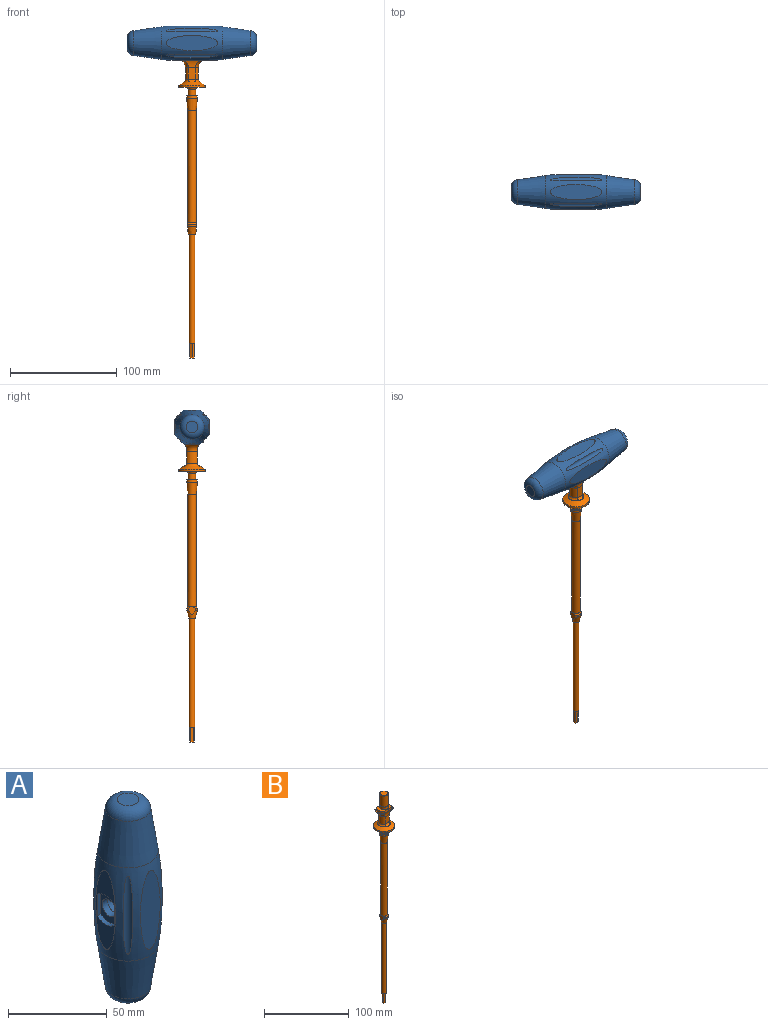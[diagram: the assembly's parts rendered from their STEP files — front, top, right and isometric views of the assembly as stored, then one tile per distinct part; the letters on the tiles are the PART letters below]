
ASSEMBLY  parts=2 mates=1
PART A: 25 faces, bbox 35x35x121 mm
  f0: plane 48.53x14.18mm, normal (-1,0,0), area 338.1mm2, adj f1,f15,f16,f17,f18
  f1: revolved ~57.74x35mm, area 3072.3mm2, adj f0,f2,f3,f8,f9,f10,f11,f12
  f2: cone r=15.37mm half-angle=8.4deg, axis (0,0,1), area 2230mm2, adj f1,f7
  f3: cone r=15.37mm half-angle=8.4deg, axis (0,0,-1), area 2230mm2, adj f1,f4
  f4: torus R=5.5mm, axis (0,0,-1), area 517mm2, adj f3,f5
  f5: plane 11x11mm, normal (0,0,1), area 95mm2, adj f4
  f6: plane 11x11mm, normal (0,0,-1), area 95mm2, adj f7
  f7: torus R=5.5mm, axis (0,0,-1), area 517mm2, adj f2,f6
  f8: plane 48.53x14.18mm, normal (1,0,0), area 537.4mm2, adj f1
  f9: plane 48.53x14.18mm, normal (0,-1,0), area 539.1mm2, adj f1
  f10: plane 48.53x14.18mm, normal (0,1,0), area 539.1mm2, adj f1
  f11: cylinder r=3mm len=48.57mm, axis (0,0,-1), area 218.5mm2, adj f1
  f12: cylinder r=3mm len=48.54mm, axis (0,0,-1), area 216.3mm2, adj f1
  f13: cylinder r=3mm len=48.56mm, axis (0,0,-1), area 221.5mm2, adj f1
  f14: cylinder r=3mm len=48.59mm, axis (0,0,-1), area 220.2mm2, adj f1
  f15: plane 13.18x2.5mm, normal (0,1,0), area 33mm2, adj f0,f16,f18,f19
  f16: cylinder r=8.98mm len=12.1mm, axis (-1,0,0), area 33.2mm2, adj f0,f15,f17,f19
  f17: plane 13.36x2.5mm, normal (0,-1,0), area 33.4mm2, adj f0,f16,f18,f19
  f18: cylinder r=8.98mm len=12.1mm, axis (-1,0,0), area 33.2mm2, adj f0,f15,f17,f19
  f19: plane 17.96x12.1mm, normal (-1,0,0), area 121mm2, adj f15,f16,f17,f18,f20
  f20: cylinder r=5mm len=10mm, axis (-1,0,0), area 125.7mm2, adj f19,f21
  f21: plane 10.25x10.25mm, normal (1,0,0), area 4mm2, adj f20,f22
  f22: cylinder r=5.12mm len=16mm, axis (-1,0,0), area 515.2mm2, adj f21,f23
  f23: cone r=4.5mm half-angle=51.3deg, axis (-1,0,0), area 24.2mm2, adj f22,f24
  f24: plane 9x9mm, normal (-1,0,0), area 63.6mm2, adj f23
PART B: 52 faces, bbox 30.3x26.3x303.4 mm
  f0: torus R=9mm, axis (0,0,1), area 52mm2, adj f8,f26,f39,f42
  f1: cylinder r=6mm len=11mm, axis (0,0,1), area 130mm2, adj f7,f9,f35,f40
  f2: torus R=13.4mm, axis (0,0,1), area 112.5mm2, adj f8,f10,f38,f43
  f3: plane 13.19x4.83mm, normal (0,0,1), area 28.7mm2, adj f4,f9,f36,f38,f43,f44
  f4: cylinder r=8.98mm len=12.02mm, axis (0,0,1), area 32.9mm2, adj f3,f6,f37,f41
  f5: cylinder r=8.98mm len=12.02mm, axis (0,0,1), area 32.9mm2, adj f6,f10,f37,f41
  f6: plane 17.96x12.02mm, normal (0,0,1), area 119.9mm2, adj f4,f5,f27,f37,f41
  f7: torus R=9mm, axis (0,0,1), area 52mm2, adj f1,f26,f39,f42
  f8: cylinder r=6mm len=11mm, axis (0,0,1), area 130mm2, adj f0,f2,f35,f40
  f9: torus R=13.4mm, axis (0,0,1), area 112.5mm2, adj f1,f3,f38,f43
  f10: plane 13.19x4.83mm, normal (0,0,1), area 28.7mm2, adj f2,f5,f36,f38,f43,f44
  f11: cone r=5mm half-angle=14deg, axis (0,0,1), area 178mm2, adj f12,f13,f17,f33,f34
  f12: cylinder r=5mm len=8mm, axis (0,0,1), area 18.5mm2, adj f11,f15,f33,f34
  f13: cylinder r=5mm len=8mm, axis (0,0,1), area 18.5mm2, adj f11,f14,f33,f34
  f14: cone r=4mm half-angle=33.7deg, axis (0,0,-1), area 20.1mm2, adj f13,f18,f33,f34
  f15: cone r=4mm half-angle=33.7deg, axis (0,0,-1), area 20.1mm2, adj f12,f18,f33,f34
  f16: cylinder r=2.7mm len=102mm, axis (0,0,1), area 1730.4mm2, adj f17,f32
  f17: plane 6x6mm, normal (0,0,-1), area 5.4mm2, adj f11,f16
  f18: cylinder r=4mm len=105mm, axis (0,0,1), area 2638.9mm2, adj f14,f15,f19
  f19: cone r=4mm half-angle=5deg, axis (0,0,1), area 326.4mm2, adj f18,f20
  f20: cylinder r=5mm len=10mm, axis (0,0,1), area 62.8mm2, adj f19,f21
  f21: plane 10x10mm, normal (0,0,1), area 40.1mm2, adj f20,f22
  f22: cylinder r=3.5mm len=7mm, axis (0,0,1), area 131.9mm2, adj f21,f23
  f23: torus R=5.5mm, axis (0,0,1), area 83.4mm2, adj f22,f24
  f24: plane 25x25mm, normal (0,0,-1), area 395.8mm2, adj f23,f25
  f25: cylinder r=12.5mm len=25mm, axis (0,0,1), area 157.1mm2, adj f24,f26
  f26: cone r=7.46mm half-angle=59.2deg, axis (0,0,-1), area 367.6mm2, adj f0,f7,f25
  f27: cylinder r=5mm len=10mm, axis (0,0,1), area 125.7mm2, adj f6,f28
  f28: plane 10.25x10.25mm, normal (0,0,-1), area 4mm2, adj f27,f29
  f29: cylinder r=5.12mm len=16mm, axis (0,0,1), area 515.2mm2, adj f28,f30
  f30: cone r=4.5mm half-angle=51.3deg, axis (0,0,-1), area 24.2mm2, adj f29,f31
  f31: plane 9x9mm, normal (0,0,1), area 63.6mm2, adj f30
  f32: plane 5.4x5.4mm, normal (0,0,-1), area 9.1mm2, adj f16,f45,f46,f47,f48,f49,f50
  f33: plane 8.82x7.32mm, normal (1,0,0), area 33.5mm2, adj f11,f12,f13,f14,f15
  f34: plane 8.38x6.88mm, normal (-1,0,0), area 33.5mm2, adj f11,f12,f13,f14,f15
  f35: plane 11x6.63mm, normal (0,1,0), area 73mm2, adj f1,f8,f38,f39
  f36: plane 13.35x0.5mm, normal (0,0,1), area 6.4mm2, adj f3,f10,f37,f38
  f37: plane 13.35x2.5mm, normal (0,1,0), area 33.3mm2, adj f4,f5,f6,f36
  f38: cylinder r=17mm len=17.74mm, axis (-1,0,0), area 70.1mm2, adj f2,f3,f9,f10,f35,f36
  f39: cylinder r=2.58mm len=6.63mm, axis (-1,0,0), area 13.1mm2, adj f0,f7,f35
  f40: plane 11x6.63mm, normal (0,-1,0), area 73mm2, adj f1,f8,f42,f43
  f41: plane 13.35x2.5mm, normal (0,-1,0), area 33.3mm2, adj f4,f5,f6,f44
  f42: cylinder r=2.58mm len=6.63mm, axis (-1,0,0), area 13.1mm2, adj f0,f7,f40
  f43: cylinder r=17mm len=17.74mm, axis (-1,0,0), area 70.1mm2, adj f2,f3,f9,f10,f40,f44
  f44: plane 13.35x0.5mm, normal (0,0,1), area 6.4mm2, adj f3,f10,f41,f43
  f45: plane 13.5x2mm, normal (0.5,-0.87,0), area 31.1mm2, adj f32,f46,f50,f51
  f46: plane 13.5x2mm, normal (-0.5,-0.87,0), area 31.1mm2, adj f32,f45,f47,f51
  f47: plane 13.5x2.31mm, normal (-1,0,0), area 31.1mm2, adj f32,f46,f48,f51
  f48: plane 13.5x2mm, normal (-0.5,0.87,0), area 31.1mm2, adj f32,f47,f49,f51
  f49: plane 13.5x2mm, normal (0.5,0.87,0), area 31.1mm2, adj f32,f48,f50,f51
  f50: plane 13.5x2.31mm, normal (1,0,0), area 31.1mm2, adj f32,f45,f49,f51
  f51: plane 4.61x4mm, normal (0,0,-1), area 13.8mm2, adj f45,f46,f47,f48,f49,f50
PLACE A rot(axis=(0,-1,0),90deg) t=(0,0,281.58)mm
PLACE B at identity fixed
MATE fastened A.f20 <-> B.f0  axis (0,0,-1) through (0,0,288.58)mm
